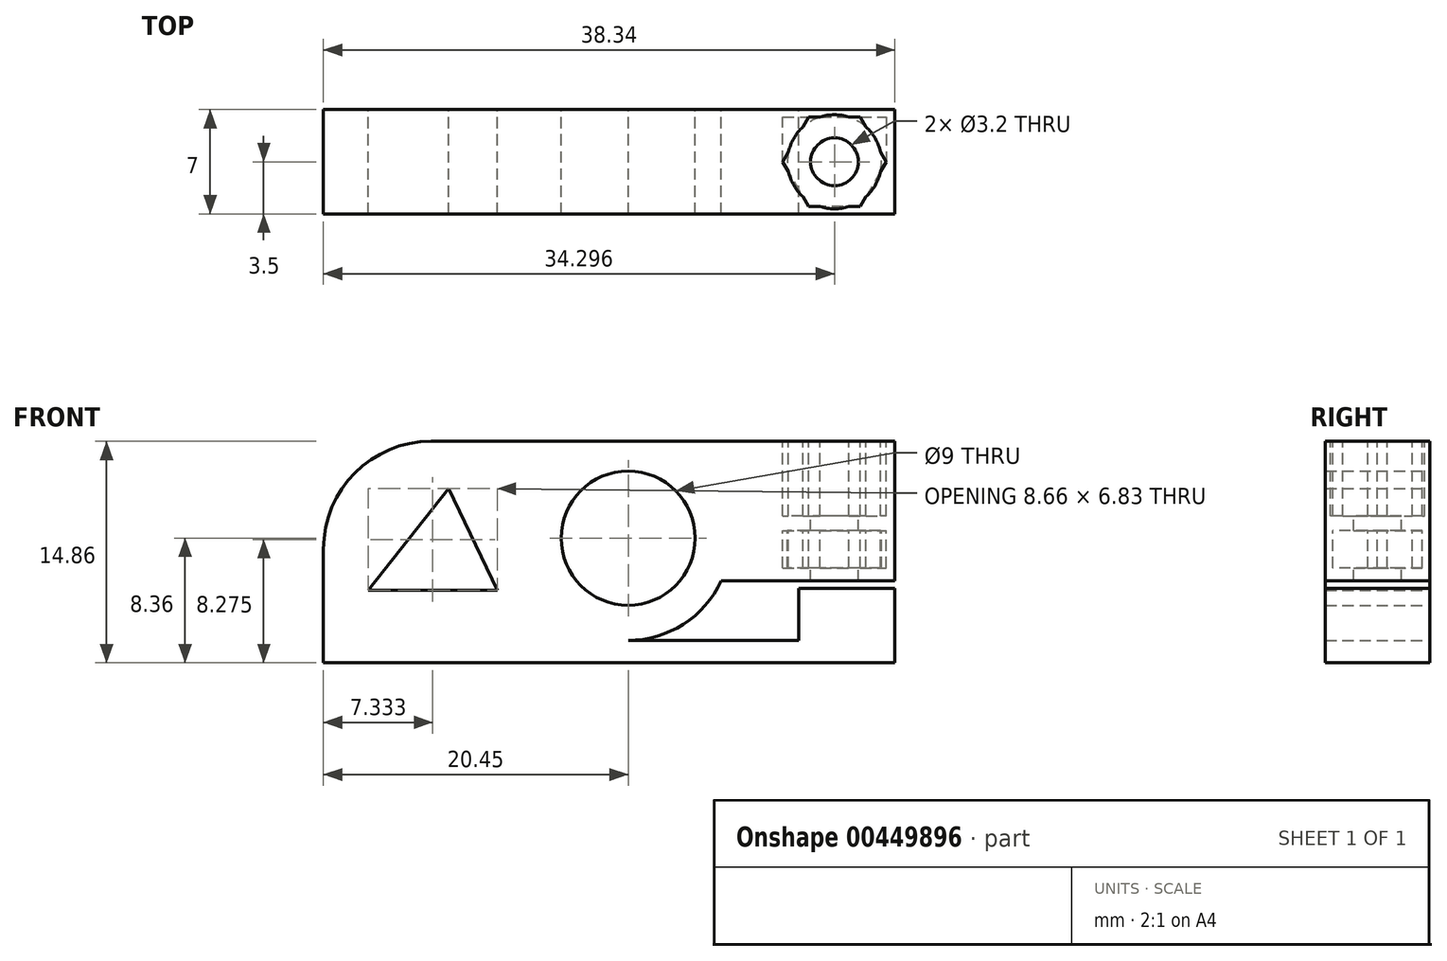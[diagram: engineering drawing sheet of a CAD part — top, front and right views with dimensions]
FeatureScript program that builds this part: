
annotation { "Feature Type Name" : "Feature", "Feature Type Description" : "" }
export const myFeature = defineFeature(function(context is Context, id is Id, definition is map)
    precondition{}
    {
        {
            var Q0;
            Q0=qCreatedBy(makeId("Front.planeOp"),FACE);
            var sketch = newSketch(context, id + "F0", { "sketchPlane" : qUnion([Q0])});
            skCircle(sketch, "E0", {"center": v(0, 0) * mm, "radius": 4.5 * mm});
            skCircle(sketch, "E1", {"center": v(0, 0) * mm, "radius": 6.5 * mm});
            skLineSegment(sketch, "E2.bottom", {"start": v(0, -6.5) * mm, "end": v(-20.45, -6.5) * mm});
            skLineSegment(sketch, "E2.top", {"start": v(0, 6.5) * mm, "end": v(-13.22, 6.5) * mm});
            skLineSegment(sketch, "E2.left", {"start": v(0, -6.5) * mm, "end": v(0, 6.5) * mm});
            skLineSegment(sketch, "E2.right", {"start": v(-20.45, -6.5) * mm, "end": v(-20.45, -0.73) * mm});
            skPoint(sketch, "E3.visualSharp", {"position": v(-20.45, 6.5) * mm});
            skArc(sketch, "E3.filletArc", {"start": v(-13.22, 6.5) * mm, "mid": v(-18.33, 4.38) * mm, "end": v(-20.45, -0.73) * mm});
            skLineSegment(sketch, "E4.bottom", {"start": v(0, -8.36) * mm, "end": v(17.89, -8.36) * mm});
            skLineSegment(sketch, "E4.top", {"start": v(0, -3.36) * mm, "end": v(17.89, -3.36) * mm});
            skLineSegment(sketch, "E4.left", {"start": v(0, -8.36) * mm, "end": v(0, -4.5) * mm});
            skLineSegment(sketch, "E4.right", {"start": v(17.89, -8.36) * mm, "end": v(17.89, -3.36) * mm});
            skLineSegment(sketch, "E5.bottom", {"start": v(0, 6.5) * mm, "end": v(17.89, 6.5) * mm});
            skLineSegment(sketch, "E5.top", {"start": v(0, -2.86) * mm, "end": v(17.89, -2.86) * mm});
            skLineSegment(sketch, "E5.left", {"start": v(0, 6.5) * mm, "end": v(0, -2.86) * mm});
            skLineSegment(sketch, "E5.right", {"start": v(17.89, 6.5) * mm, "end": v(17.89, -2.86) * mm});
            skLineSegment(sketch, "E6.bottom", {"start": v(-20.45, -6.5) * mm, "end": v(0, -6.5) * mm});
            skLineSegment(sketch, "E6.top", {"start": v(-20.45, -8.36) * mm, "end": v(0, -8.36) * mm});
            skLineSegment(sketch, "E6.left", {"start": v(-20.45, -6.5) * mm, "end": v(-20.45, -8.36) * mm});
            skLineSegment(sketch, "E6.right", {"start": v(0, -6.5) * mm, "end": v(0, -8.36) * mm});
            skLineSegment(sketch, "E7", {"start": v(0, -6.86) * mm, "end": v(11.44, -6.86) * mm});
            skLineSegment(sketch, "E8", {"start": v(11.44, -6.86) * mm, "end": v(11.44, -3.36) * mm});
            skLineSegment(sketch, "E9", {"start": v(-17.45, -3.5) * mm, "end": v(-12.03, 3.33) * mm});
            skLineSegment(sketch, "E10", {"start": v(-12.03, 3.33) * mm, "end": v(-8.79, -3.5) * mm});
            skLineSegment(sketch, "E11", {"start": v(-8.79, -3.5) * mm, "end": v(-17.45, -3.5) * mm});
            skArc(sketch, "E12", {"start": v(-2.2, 6.5) * mm, "mid": v(0, -6.86) * mm, "end": v(2.2, 6.5) * mm});
            skSolve(sketch);
        }
        {
            var Q0;
            {var subQ0=sQuery(id+"F0.wireOp",EDGE,"E2.bottom");Q0=makeQuery(id+"F0.imprint","IMPRINT",FACE,{"disambiguationData":[TD([[makeQuery(id+"F0.imprint","IMPRINT",EDGE,{"derivedFrom":subQ0}),-1.0]])]});}
            var Q1;
            {var subQ0=sQuery(id+"F0.wireOp",EDGE,"E4.left");Q1=makeQuery(id+"F0.imprint","IMPRINT",FACE,{"disambiguationData":[TD([[makeQuery(id+"F0.imprint","IMPRINT",EDGE,{"derivedFrom":subQ0}),1.0]])]});}
            var Q2;
            {var subQ0=sQuery(id+"F0.wireOp",EDGE,"E4.left");Q2=makeQuery(id+"F0.imprint","IMPRINT",FACE,{"disambiguationData":[TD([[makeQuery(id+"F0.imprint","IMPRINT",EDGE,{"derivedFrom":subQ0}),-1.0]])]});}
            var Q3;
            {var subQ0=sQuery(id+"F0.wireOp",EDGE,"E4.top");var subQ5=sQuery(id+"F0.wireOp",EDGE,"E1");var subQ6=makeQuery(id+"F0.imprint","INTERSECT",VERTEX,{"derivedFrom":[subQ5,subQ0]});Q3=makeQuery(id+"F0.imprint","IMPRINT",FACE,{"disambiguationData":[TD([[makeQuery(id+"F0.imprint","IMPRINT",EDGE,{"disambiguationData":[TD([[subQ6,-1.0]])],"derivedFrom":subQ5}),1.0]])]});}
            var Q4;
            {var subQ0=sQuery(id+"F0.wireOp",EDGE,"E5.left");var subQ1=sQuery(id+"F0.wireOp",EDGE,"E0");var subQ2=makeQuery(id+"F0.imprint","INTERSECT",VERTEX,{"derivedFrom":[subQ1,subQ0]});Q4=makeQuery(id+"F0.imprint","IMPRINT",FACE,{"disambiguationData":[TD([[makeQuery(id+"F0.imprint","IMPRINT",EDGE,{"disambiguationData":[TD([[subQ2,1.0]])],"derivedFrom":subQ1}),-1.0]])]});}
            var Q5;
            {var subQ0=sQuery(id+"F0.wireOp",EDGE,"E5.bottom");Q5=makeQuery(id+"F0.imprint","IMPRINT",FACE,{"disambiguationData":[TD([[makeQuery(id+"F0.imprint","IMPRINT",EDGE,{"derivedFrom":subQ0}),-1.0]])]});}
            var Q6;
            {var subQ0=sQuery(id+"F0.wireOp",EDGE,"E4.bottom");Q6=makeQuery(id+"F0.imprint","IMPRINT",FACE,{"disambiguationData":[TD([[makeQuery(id+"F0.imprint","IMPRINT",EDGE,{"derivedFrom":subQ0}),1.0]])]});}
            var Q7;
            {var subQ0=sQuery(id+"F0.wireOp",EDGE,"E2.top");Q7=makeQuery(id+"F0.imprint","IMPRINT",FACE,{"disambiguationData":[TD([[makeQuery(id+"F0.imprint","IMPRINT",EDGE,{"derivedFrom":subQ0}),1.0]])]});}
            var Q8;
            Q8=makeQuery(id+"F0.imprint","IMPRINT",FACE,{"disambiguationData":[TD([[makeQuery(id+"F0.imprint","IMPRINT",EDGE,{"derivedFrom":sQuery(id+"F0.wireOp",EDGE,"E6.bottom")}),-1.0]])]});
            var Q9;
            {var subQ5=sQuery(id+"F0.wireOp",EDGE,"E4.top");var subQ6=sQuery(id+"F0.wireOp",EDGE,"E1");var subQ7=makeQuery(id+"F0.imprint","INTERSECT",VERTEX,{"derivedFrom":[subQ6,subQ5]});Q9=makeQuery(id+"F0.imprint","IMPRINT",FACE,{"disambiguationData":[TD([[makeQuery(id+"F0.imprint","IMPRINT",EDGE,{"disambiguationData":[TD([[subQ7,1.0]])],"derivedFrom":subQ6}),1.0]])]});}
            var Q10;
            {var subQ1=sQuery(id+"F0.wireOp",EDGE,"E6.top");Q10=makeQuery(id+"F0.imprint","IMPRINT",FACE,{"disambiguationData":[TD([[makeQuery(id+"F0.imprint","IMPRINT",EDGE,{"derivedFrom":subQ1}),1.0]])]});}
            var Q11;
            {var subQ1=sQuery(id+"F0.wireOp",EDGE,"E2.right");Q11=makeQuery(id+"F0.imprint","IMPRINT",FACE,{"disambiguationData":[TD([[makeQuery(id+"F0.imprint","IMPRINT",EDGE,{"derivedFrom":subQ1}),-1.0]])]});}
            var Q12;
            {var subQ3=sQuery(id+"F0.wireOp",EDGE,"E4.top");var subQ5=sQuery(id+"F0.wireOp",EDGE,"E12");var subQ7=makeQuery(id+"F0.imprint","INTERSECT",VERTEX,{"derivedFrom":[subQ3,subQ5]});Q12=makeQuery(id+"F0.imprint","IMPRINT",FACE,{"disambiguationData":[TD([[makeQuery(id+"F0.imprint","IMPRINT",EDGE,{"disambiguationData":[TD([[subQ7,1.0]])],"derivedFrom":subQ3}),-1.0]])]});}
            var Q13;
            {var subQ0=sQuery(id+"F0.wireOp",EDGE,"E4.top");var subQ1=sQuery(id+"F0.wireOp",EDGE,"E1");var subQ2=makeQuery(id+"F0.imprint","INTERSECT",VERTEX,{"derivedFrom":[subQ1,subQ0]});Q13=makeQuery(id+"F0.imprint","IMPRINT",FACE,{"disambiguationData":[TD([[makeQuery(id+"F0.imprint","IMPRINT",EDGE,{"disambiguationData":[TD([[subQ2,-1.0]])],"derivedFrom":subQ1}),-1.0]])]});}
            extrude(context, id + "F1", {"entities" : qUnion([Q0, Q1, Q2, Q3, Q4, Q5, Q6, Q7, Q8, Q9, Q10, Q11, Q12, Q13]), "depth" : 7 * mm});
        }
        {
            var Q0;
            Q0=makeQuery(id+"F1.opExtrude","SWEPT_FACE",FACE,{"disambiguationData":[OSD([sQuery(id+"F0.wireOp",EDGE,"E2.top"),sQuery(id+"F0.wireOp",EDGE,"E5.bottom")])]});
            var sketch = newSketch(context, id + "F2", { "sketchPlane" : qUnion([Q0])});
            skLineSegment(sketch, "E13", {"start": v(2.33, -7) * mm, "end": v(2.33, 0) * mm, "construction": true});
            skLineSegment(sketch, "E14", {"start": v(17.89, 0) * mm, "end": v(9.8, -7) * mm, "construction": true});
            skLineSegment(sketch, "E15", {"start": v(9.8, -7) * mm, "end": v(9.8, 0) * mm, "construction": true});
            skLineSegment(sketch, "E16", {"start": v(9.8, 0) * mm, "end": v(17.89, -7) * mm, "construction": true});
            skCircle(sketch, "E17.cCircle", {"center": v(13.85, -3.5) * mm, "radius": 3 * mm, "construction": true});
            skLineSegment(sketch, "E17.0", {"start": v(15.58, -6.5) * mm, "end": v(12.11, -6.5) * mm});
            skLineSegment(sketch, "E17.1", {"start": v(12.11, -6.5) * mm, "end": v(10.38, -3.5) * mm});
            skLineSegment(sketch, "E17.2", {"start": v(10.38, -3.5) * mm, "end": v(12.11, -0.5) * mm});
            skLineSegment(sketch, "E17.3", {"start": v(12.11, -0.5) * mm, "end": v(15.58, -0.5) * mm});
            skLineSegment(sketch, "E17.4", {"start": v(15.58, -0.5) * mm, "end": v(17.31, -3.5) * mm});
            skLineSegment(sketch, "E17.5", {"start": v(17.31, -3.5) * mm, "end": v(15.58, -6.5) * mm});
            skPoint(sketch, "E17.0.midPoint", {"position": v(13.85, -6.5) * mm});
            skCircle(sketch, "E18", {"center": v(13.85, -3.5) * mm, "radius": 1.6 * mm});
            skLineSegment(sketch, "E19", {"start": v(10.38, -3.5) * mm, "end": v(10.38, -0.5) * mm});
            skLineSegment(sketch, "E20", {"start": v(10.38, -0.5) * mm, "end": v(12.11, -0.5) * mm});
            skLineSegment(sketch, "E21", {"start": v(15.58, -0.5) * mm, "end": v(17.3, -0.5) * mm});
            skLineSegment(sketch, "E22", {"start": v(17.3, -0.5) * mm, "end": v(17.31, -3.5) * mm});
            skCircle(sketch, "E23", {"center": v(13.85, -3.5) * mm, "radius": 3.15 * mm});
            skSolve(sketch);
        }
        {
            var Q0;
            Q0=makeQuery(id+"F2.imprint","IMPRINT",FACE,{"disambiguationData":[TD([[makeQuery(id+"F2.imprint","IMPRINT",EDGE,{"derivedFrom":sQuery(id+"F2.wireOp",EDGE,"E18")}),1.0]])]});
            extrude(context, id + "F3", {"entities" : qUnion([Q0]), "operationType" : NewBodyOperationType.REMOVE, "oppositeDirection" : true, "depth" : 9.7 * mm});
        }
        {
            var Q0;
            Q0=makeQuery(id+"F2.imprint","IMPRINT",FACE,{"disambiguationData":[TD([[makeQuery(id+"F2.imprint","IMPRINT",EDGE,{"derivedFrom":sQuery(id+"F2.wireOp",EDGE,"E17.0")}),-1.0]])]});
            var Q1;
            Q1=makeQuery(id+"F2.imprint","IMPRINT",FACE,{"disambiguationData":[TD([[makeQuery(id+"F2.imprint","IMPRINT",EDGE,{"derivedFrom":sQuery(id+"F2.wireOp",EDGE,"E17.2")}),1.0]])]});
            var Q2;
            {var subQ0=sQuery(id+"F2.wireOp",EDGE,"E23");var subQ1=sQuery(id+"F2.wireOp",EDGE,"E17.2");var subQ2=makeQuery(id+"F2.imprint","INTERSECT",VERTEX,{"disambiguationData":[OD(0.0)],"derivedFrom":[subQ1,subQ0]});Q2=makeQuery(id+"F2.imprint","IMPRINT",FACE,{"disambiguationData":[TD([[makeQuery(id+"F2.imprint","IMPRINT",EDGE,{"disambiguationData":[TD([[subQ2,-1.0]])],"derivedFrom":subQ1}),1.0]])]});}
            var Q3;
            Q3=makeQuery(id+"F2.imprint","IMPRINT",FACE,{"disambiguationData":[TD([[makeQuery(id+"F2.imprint","IMPRINT",EDGE,{"derivedFrom":sQuery(id+"F2.wireOp",EDGE,"E18")}),-1.0]])]});
            var Q4;
            {var subQ0=sQuery(id+"F2.wireOp",EDGE,"E23");var subQ1=sQuery(id+"F2.wireOp",EDGE,"E17.4");var subQ2=makeQuery(id+"F2.imprint","INTERSECT",VERTEX,{"disambiguationData":[OD(0.0)],"derivedFrom":[subQ1,subQ0]});Q4=makeQuery(id+"F2.imprint","IMPRINT",FACE,{"disambiguationData":[TD([[makeQuery(id+"F2.imprint","IMPRINT",EDGE,{"disambiguationData":[TD([[subQ2,-1.0]])],"derivedFrom":subQ1}),1.0]])]});}
            var Q5;
            {var subQ0=sQuery(id+"F2.wireOp",EDGE,"E21");Q5=makeQuery(id+"F2.imprint","IMPRINT",FACE,{"disambiguationData":[TD([[makeQuery(id+"F2.imprint","IMPRINT",EDGE,{"derivedFrom":subQ0}),-1.0]])]});}
            extrude(context, id + "F4", {"entities" : qUnion([Q0, Q1, Q2, Q3, Q4, Q5]), "operationType" : NewBodyOperationType.REMOVE, "oppositeDirection" : true, "depth" : 8.5 * mm, "hasSecondDirection" : true, "secondDirectionOppositeDirection" : true, "secondDirectionDepth" : 6 * mm});
        }
        {
            var Q0;
            {var subQ0=sQuery(id+"F2.wireOp",EDGE,"E17.5");var subQ1=sQuery(id+"F2.wireOp",EDGE,"E17.0");var subQ2=makeQuery(id+"F2.imprint","INTERSECT",VERTEX,{"derivedFrom":[subQ1,subQ0]});Q0=makeQuery(id+"F2.imprint","IMPRINT",FACE,{"disambiguationData":[TD([[makeQuery(id+"F2.imprint","IMPRINT",EDGE,{"disambiguationData":[TD([[subQ2,-1.0]])],"derivedFrom":subQ1}),-1.0]])]});}
            var Q1;
            {var subQ0=sQuery(id+"F2.wireOp",EDGE,"E23");var subQ1=sQuery(id+"F2.wireOp",EDGE,"E17.0");var subQ2=makeQuery(id+"F2.imprint","INTERSECT",VERTEX,{"disambiguationData":[OD(0.0)],"derivedFrom":[subQ1,subQ0]});Q1=makeQuery(id+"F2.imprint","IMPRINT",FACE,{"disambiguationData":[TD([[makeQuery(id+"F2.imprint","IMPRINT",EDGE,{"disambiguationData":[TD([[subQ2,-1.0]])],"derivedFrom":subQ1}),1.0]])]});}
            var Q2;
            {var subQ0=sQuery(id+"F2.wireOp",EDGE,"E17.1");var subQ1=sQuery(id+"F2.wireOp",EDGE,"E17.0");var subQ2=makeQuery(id+"F2.imprint","INTERSECT",VERTEX,{"derivedFrom":[subQ1,subQ0]});Q2=makeQuery(id+"F2.imprint","IMPRINT",FACE,{"disambiguationData":[TD([[makeQuery(id+"F2.imprint","IMPRINT",EDGE,{"disambiguationData":[TD([[subQ2,1.0]])],"derivedFrom":subQ1}),-1.0]])]});}
            var Q3;
            {var subQ0=sQuery(id+"F2.wireOp",EDGE,"E23");var subQ1=sQuery(id+"F2.wireOp",EDGE,"E17.1");var subQ2=makeQuery(id+"F2.imprint","INTERSECT",VERTEX,{"disambiguationData":[OD(0.0)],"derivedFrom":[subQ1,subQ0]});Q3=makeQuery(id+"F2.imprint","IMPRINT",FACE,{"disambiguationData":[TD([[makeQuery(id+"F2.imprint","IMPRINT",EDGE,{"disambiguationData":[TD([[subQ2,-1.0]])],"derivedFrom":subQ1}),1.0]])]});}
            var Q4;
            {var subQ0=sQuery(id+"F2.wireOp",EDGE,"E23");var subQ1=sQuery(id+"F2.wireOp",EDGE,"E17.3");var subQ2=makeQuery(id+"F2.imprint","INTERSECT",VERTEX,{"disambiguationData":[OD(0.0)],"derivedFrom":[subQ1,subQ0]});Q4=makeQuery(id+"F2.imprint","IMPRINT",FACE,{"disambiguationData":[TD([[makeQuery(id+"F2.imprint","IMPRINT",EDGE,{"disambiguationData":[TD([[subQ2,-1.0]])],"derivedFrom":subQ1}),1.0]])]});}
            var Q5;
            {var subQ0=sQuery(id+"F2.wireOp",EDGE,"E23");var subQ1=sQuery(id+"F2.wireOp",EDGE,"E17.5");var subQ2=makeQuery(id+"F2.imprint","INTERSECT",VERTEX,{"disambiguationData":[OD(0.0)],"derivedFrom":[subQ1,subQ0]});Q5=makeQuery(id+"F2.imprint","IMPRINT",FACE,{"disambiguationData":[TD([[makeQuery(id+"F2.imprint","IMPRINT",EDGE,{"disambiguationData":[TD([[subQ2,-1.0]])],"derivedFrom":subQ1}),1.0]])]});}
            var Q6;
            {var subQ1=sQuery(id+"F2.wireOp",EDGE,"E17.1");var subQ3=sQuery(id+"F2.wireOp",EDGE,"E23");var subQ4=makeQuery(id+"F2.imprint","INTERSECT",VERTEX,{"disambiguationData":[OD(1.0)],"derivedFrom":[subQ1,subQ3]});Q6=makeQuery(id+"F2.imprint","IMPRINT",FACE,{"disambiguationData":[TD([[makeQuery(id+"F2.imprint","IMPRINT",EDGE,{"disambiguationData":[TD([[subQ4,1.0]])],"derivedFrom":subQ3}),-1.0]])]});}
            var Q7;
            {var subQ1=sQuery(id+"F2.wireOp",EDGE,"E17.2");var subQ3=sQuery(id+"F2.wireOp",EDGE,"E23");var subQ4=makeQuery(id+"F2.imprint","INTERSECT",VERTEX,{"disambiguationData":[OD(1.0)],"derivedFrom":[subQ1,subQ3]});Q7=makeQuery(id+"F2.imprint","IMPRINT",FACE,{"disambiguationData":[TD([[makeQuery(id+"F2.imprint","IMPRINT",EDGE,{"disambiguationData":[TD([[subQ4,1.0]])],"derivedFrom":subQ3}),-1.0]])]});}
            var Q8;
            {var subQ1=sQuery(id+"F2.wireOp",EDGE,"E17.3");var subQ3=sQuery(id+"F2.wireOp",EDGE,"E23");var subQ4=makeQuery(id+"F2.imprint","INTERSECT",VERTEX,{"disambiguationData":[OD(1.0)],"derivedFrom":[subQ1,subQ3]});Q8=makeQuery(id+"F2.imprint","IMPRINT",FACE,{"disambiguationData":[TD([[makeQuery(id+"F2.imprint","IMPRINT",EDGE,{"disambiguationData":[TD([[subQ4,1.0]])],"derivedFrom":subQ3}),-1.0]])]});}
            var Q9;
            {var subQ1=sQuery(id+"F2.wireOp",EDGE,"E17.4");var subQ3=sQuery(id+"F2.wireOp",EDGE,"E23");var subQ4=makeQuery(id+"F2.imprint","INTERSECT",VERTEX,{"disambiguationData":[OD(1.0)],"derivedFrom":[subQ1,subQ3]});Q9=makeQuery(id+"F2.imprint","IMPRINT",FACE,{"disambiguationData":[TD([[makeQuery(id+"F2.imprint","IMPRINT",EDGE,{"disambiguationData":[TD([[subQ4,1.0]])],"derivedFrom":subQ3}),-1.0]])]});}
            var Q10;
            Q10=makeQuery(id+"F2.imprint","IMPRINT",FACE,{"disambiguationData":[TD([[makeQuery(id+"F2.imprint","IMPRINT",EDGE,{"derivedFrom":sQuery(id+"F2.wireOp",EDGE,"E18")}),-1.0]])]});
            var Q11;
            {var subQ0=sQuery(id+"F2.wireOp",EDGE,"E23");var subQ1=sQuery(id+"F2.wireOp",EDGE,"E17.4");var subQ2=makeQuery(id+"F2.imprint","INTERSECT",VERTEX,{"disambiguationData":[OD(0.0)],"derivedFrom":[subQ1,subQ0]});Q11=makeQuery(id+"F2.imprint","IMPRINT",FACE,{"disambiguationData":[TD([[makeQuery(id+"F2.imprint","IMPRINT",EDGE,{"disambiguationData":[TD([[subQ2,-1.0]])],"derivedFrom":subQ1}),1.0]])]});}
            var Q12;
            {var subQ0=sQuery(id+"F2.wireOp",EDGE,"E23");var subQ1=sQuery(id+"F2.wireOp",EDGE,"E17.2");var subQ2=makeQuery(id+"F2.imprint","INTERSECT",VERTEX,{"disambiguationData":[OD(0.0)],"derivedFrom":[subQ1,subQ0]});Q12=makeQuery(id+"F2.imprint","IMPRINT",FACE,{"disambiguationData":[TD([[makeQuery(id+"F2.imprint","IMPRINT",EDGE,{"disambiguationData":[TD([[subQ2,-1.0]])],"derivedFrom":subQ1}),1.0]])]});}
            extrude(context, id + "F5", {"entities" : qUnion([Q0, Q1, Q2, Q3, Q4, Q5, Q6, Q7, Q8, Q9, Q10, Q11, Q12]), "operationType" : NewBodyOperationType.REMOVE, "oppositeDirection" : true, "depth" : 5 * mm});
        }
    });
